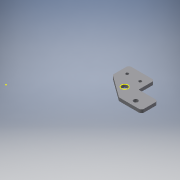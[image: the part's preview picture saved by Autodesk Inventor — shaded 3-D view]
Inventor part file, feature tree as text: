
AUTODESK INVENTOR PART (.ipt)
format: ipt  version: 2017 (Build 210142000, 142)  size: 245,760 bytes
history: native  units: mm
features: other x3, sketch x3, extrude x1
ambient origin geometry x8: Origin, YZ Plane, XZ Plane, XY Plane, X Axis, Y Axis, Z Axis, Center Point
bodies: Solid1 (feature_tree)
feature tree (7):
  other  "Leadscrew-rod-holder.ipt"
  extrude  "Extrusion1"  Depth=10.0mm TaperAngle=0.0deg
  other  "Solid1::Leadscrew-rod-holder.ipt"
  other  "TaggingFeature1"
  sketch  "Sketch1"  dims[d0=10.0mm d1=10.0mm d2=0.0mm]
  sketch  "Sketch2"  dims[d3=12.3mm]
  sketch  "Sketch3"
